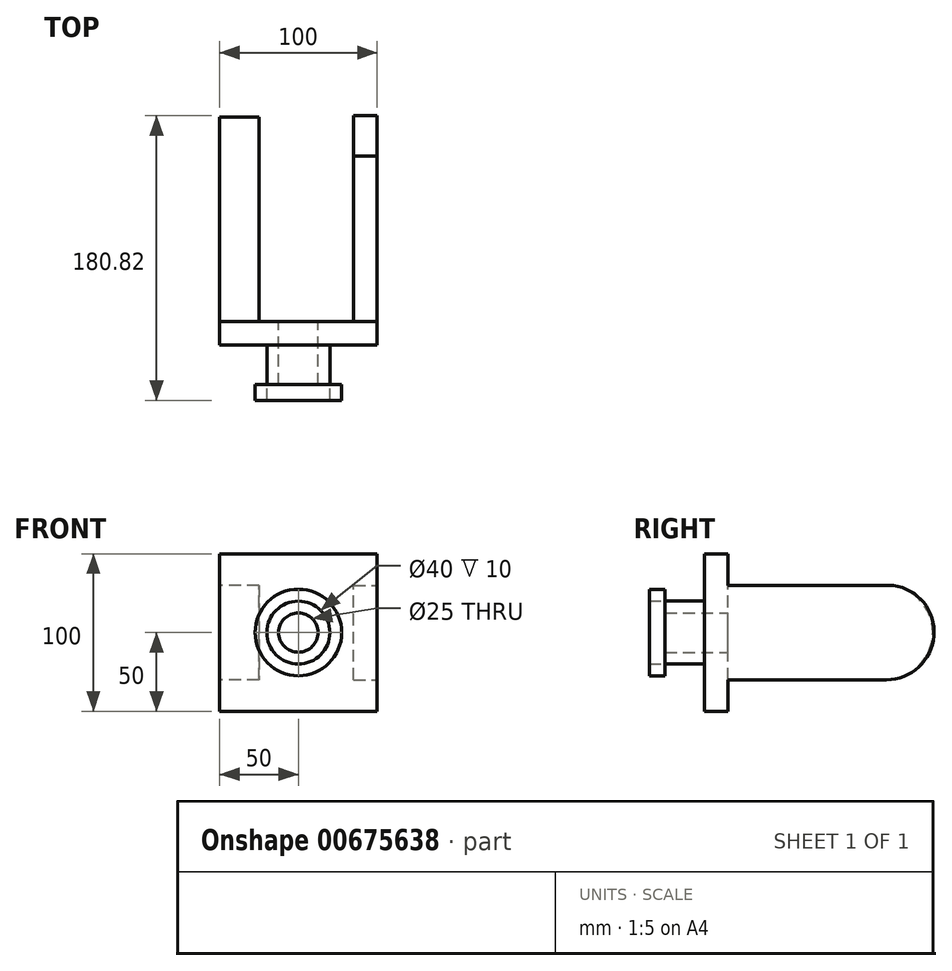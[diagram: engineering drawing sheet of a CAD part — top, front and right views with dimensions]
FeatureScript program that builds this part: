
annotation { "Feature Type Name" : "Feature", "Feature Type Description" : "" }
export const myFeature = defineFeature(function(context is Context, id is Id, definition is map)
    precondition{}
    {
        {
            var Q0;
            Q0=qCreatedBy(makeId("Front.planeOp"),FACE);
            var sketch = newSketch(context, id + "F0", { "sketchPlane" : qUnion([Q0])});
            skLineSegment(sketch, "E0.bottom", {"start": v(0, 0) * mm, "end": v(100, 0) * mm});
            skLineSegment(sketch, "E0.top", {"start": v(0, 100) * mm, "end": v(100, 100) * mm});
            skLineSegment(sketch, "E0.left", {"start": v(0, 0) * mm, "end": v(0, 100) * mm});
            skLineSegment(sketch, "E0.right", {"start": v(100, 0) * mm, "end": v(100, 100) * mm});
            skCircle(sketch, "E1", {"center": v(50, 50) * mm, "radius": 12.5 * mm});
            skPoint(sketch, "E1.centerSnap0", {"position": v(0, 50) * mm});
            skPoint(sketch, "E1.centerSnap1", {"position": v(50, 100) * mm});
            skCircle(sketch, "E2", {"center": v(50, 50) * mm, "radius": 20 * mm});
            skSolve(sketch);
        }
        {
            var Q0;
            Q0 = qSketchRegion(id + "F0", true);
            extrude(context, id + "F1", {"entities" : qUnion([Q0]), "depth" : 15 * mm, "offsetDistance" : 25 * mm});
        }
        {
            var Q0;
            Q0=makeQuery(id+"F0.imprint","IMPRINT",FACE,{"disambiguationData":[TD([[makeQuery(id+"F0.imprint","IMPRINT",EDGE,{"derivedFrom":sQuery(id+"F0.wireOp",EDGE,"E1")}),-1.0]])]});
            extrude(context, id + "F2", {"entities" : qUnion([Q0]), "operationType" : NewBodyOperationType.ADD, "depth" : 40 * mm, "offsetDistance" : 25 * mm});
        }
        {
            var Q0;
            Q0=makeQuery(id+"F2.opExtrude","CAP_FACE",FACE,{"disambiguationData":[OSD([sQuery(id+"F0.wireOp",EDGE,"E1"),sQuery(id+"F0.wireOp",EDGE,"E2")])],"isStart":false});
            var sketch = newSketch(context, id + "F3", { "sketchPlane" : qUnion([Q0])});
            skCircle(sketch, "E3", {"center": v(50, 50) * mm, "radius": 27.5 * mm});
            skCircle(sketch, "E4", {"center": v(50, 50) * mm, "radius": 20 * mm});
            skSolve(sketch);
        }
        {
            var Q0;
            Q0 = qSketchRegion(id + "F3", true);
            extrude(context, id + "F4", {"entities" : qUnion([Q0]), "operationType" : NewBodyOperationType.ADD, "depth" : 10 * mm, "offsetDistance" : 25 * mm});
        }
        {
            var Q0;
            Q0=makeQuery(id+"F1.opExtrude","SWEPT_FACE",FACE,{"disambiguationData":[OSD([sQuery(id+"F0.wireOp",EDGE,"E0.right")])]});
            var sketch = newSketch(context, id + "F5", { "sketchPlane" : qUnion([Q0])});
            skLineSegment(sketch, "E5", {"start": v(0, 80) * mm, "end": v(105.16, 80) * mm});
            skLineSegment(sketch, "E6", {"start": v(0, 20) * mm, "end": v(100.65, 20) * mm});
            skArc(sketch, "E7", {"start": v(100.65, 20) * mm, "mid": v(130.74, 47.9) * mm, "end": v(105.16, 80) * mm});
            skSolve(sketch);
        }
        {
            var Q0;
            {var subQ0=sQuery(id+"F5.wireOp",EDGE,"E5");Q0=makeQuery(id+"F5.imprint","IMPRINT",FACE,{"disambiguationData":[TD([[makeQuery(id+"F5.imprint","IMPRINT",EDGE,{"derivedFrom":subQ0}),-1.0]])]});}
            var Q1;
            {var subQ0=sQuery(id+"F0.wireOp",EDGE,"E2");Q1=makeQuery(id+"F2.boolean.opBoolean","MERGE",FACE,{"derivedFrom":[makeQuery(id+"F1.opExtrude","CAP_FACE",FACE,{"disambiguationData":[OSD([sQuery(id+"F0.wireOp",EDGE,"E0.bottom"),sQuery(id+"F0.wireOp",EDGE,"E0.top"),sQuery(id+"F0.wireOp",EDGE,"E0.left"),sQuery(id+"F0.wireOp",EDGE,"E0.right"),subQ0])],"isStart":true}),makeQuery(id+"F2.opExtrude","CAP_FACE",FACE,{"disambiguationData":[OSD([sQuery(id+"F0.wireOp",EDGE,"E1"),subQ0])],"isStart":true})]});}
            extrude(context, id + "F6", {"entities" : qUnion([Q0]), "operationType" : NewBodyOperationType.ADD, "oppositeDirection" : true, "depth" : 15 * mm, "endBoundEntityFace" : qUnion([Q1]), "offsetDistance" : 25 * mm});
        }
        {
            var Q0;
            Q0=makeQuery(id+"F1.opExtrude","SWEPT_FACE",FACE,{"disambiguationData":[OSD([sQuery(id+"F0.wireOp",EDGE,"E0.left")])]});
            var sketch = newSketch(context, id + "F7", { "sketchPlane" : qUnion([Q0])});
            skLineSegment(sketch, "E8", {"start": v(0, 80) * mm, "end": v(-100, 80) * mm});
            skLineSegment(sketch, "E9", {"start": v(0, 20) * mm, "end": v(-100, 20) * mm});
            skArc(sketch, "E10", {"start": v(-100, 80) * mm, "mid": v(-130, 50) * mm, "end": v(-100, 20) * mm});
            skSolve(sketch);
        }
        {
            var Q0;
            {var subQ0=sQuery(id+"F7.wireOp",EDGE,"E8");Q0=makeQuery(id+"F7.imprint","IMPRINT",FACE,{"disambiguationData":[TD([[makeQuery(id+"F7.imprint","IMPRINT",EDGE,{"derivedFrom":subQ0}),1.0]])]});}
            extrude(context, id + "F8", {"entities" : qUnion([Q0]), "operationType" : NewBodyOperationType.ADD, "oppositeDirection" : true, "depth" : 25 * mm, "offsetDistance" : 25 * mm});
        }
    });
